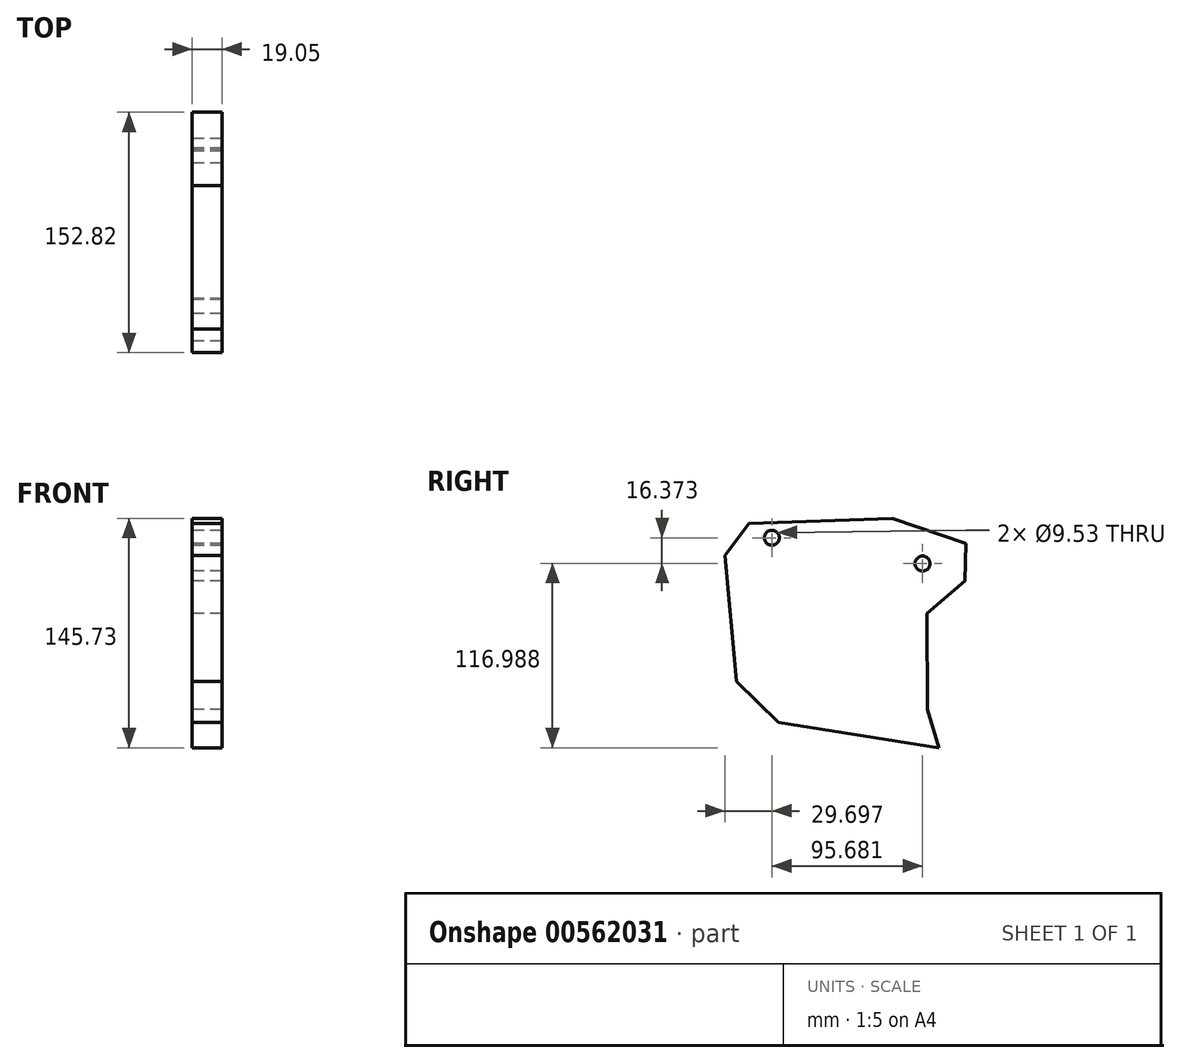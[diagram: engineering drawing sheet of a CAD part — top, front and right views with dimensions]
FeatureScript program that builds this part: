
annotation { "Feature Type Name" : "Feature", "Feature Type Description" : "" }
export const myFeature = defineFeature(function(context is Context, id is Id, definition is map)
    precondition{}
    {
        {
            var Q0;
            Q0=qCreatedBy(makeId("Right.planeOp"),FACE);
            var sketch = newSketch(context, id + "F0", { "sketchPlane" : qUnion([Q0])});
            skLineSegment(sketch, "E0", {"start": v(-513.86, 319.86) * mm, "end": v(-513.86, 78.56) * mm});
            skSolve(sketch);
        }
        {
            var Q0;
            Q0=qCreatedBy(makeId("Right.planeOp"),FACE);
            var sketch = newSketch(context, id + "F1", { "sketchPlane" : qUnion([Q0])});
            skLineSegment(sketch, "E1", {"start": v(-749.74, 255.74) * mm, "end": v(-601.81, 261.03) * mm});
            skLineSegment(sketch, "E2", {"start": v(-562.23, 653.83) * mm, "end": v(-601.81, 261.03) * mm});
            skLineSegment(sketch, "E3", {"start": v(-562.23, 653.83) * mm, "end": v(-749.74, 255.74) * mm});
            skLineSegment(sketch, "E4", {"start": v(-712.77, 291.22) * mm, "end": v(-724.73, 436.34) * mm});
            skLineSegment(sketch, "E5", {"start": v(-712.77, 291.22) * mm, "end": v(-827.95, 541.82) * mm});
            skLineSegment(sketch, "E6", {"start": v(-724.73, 436.34) * mm, "end": v(-827.95, 541.82) * mm});
            skLineSegment(sketch, "E7", {"start": v(-1010.55, 658.15) * mm, "end": v(-827.95, 541.82) * mm});
            skLineSegment(sketch, "E8", {"start": v(-1039.87, 675.04) * mm, "end": v(-1010.55, 658.15) * mm});
            skLineSegment(sketch, "E9", {"start": v(-1039.87, 675.04) * mm, "end": v(-712.77, 291.22) * mm});
            skLineSegment(sketch, "E10", {"start": v(-1010.55, 658.15) * mm, "end": v(-712.77, 291.22) * mm});
            skLineSegment(sketch, "E11", {"start": v(-601.81, 261.03) * mm, "end": v(-596.02, 401.8) * mm});
            skLineSegment(sketch, "E12", {"start": v(-601.81, 261.03) * mm, "end": v(-610.07, 655.83) * mm});
            skLineSegment(sketch, "E13", {"start": v(-596.02, 401.8) * mm, "end": v(-610.07, 655.83) * mm});
            skLineSegment(sketch, "E14", {"start": v(-724.73, 436.34) * mm, "end": v(-596.02, 401.8) * mm});
            skLineSegment(sketch, "E15", {"start": v(-827.95, 541.82) * mm, "end": v(-776.44, 589.47) * mm});
            skLineSegment(sketch, "E16", {"start": v(-749.74, 255.74) * mm, "end": v(-776.44, 589.47) * mm});
            skLineSegment(sketch, "E17", {"start": v(-1044.3, 791.08) * mm, "end": v(-776.44, 589.47) * mm});
            skLineSegment(sketch, "E18", {"start": v(-1392.7, 315.05) * mm, "end": v(-1338.72, 358.03) * mm});
            skLineSegment(sketch, "E19", {"start": v(-1338.72, 358.03) * mm, "end": v(-1297.02, 298.68) * mm});
            skLineSegment(sketch, "E20", {"start": v(-1044.3, 791.08) * mm, "end": v(-1297.02, 298.68) * mm});
            skLineSegment(sketch, "E21", {"start": v(-1297.02, 298.68) * mm, "end": v(-1039.87, 675.04) * mm});
            skLineSegment(sketch, "E22", {"start": v(-1039.87, 675.04) * mm, "end": v(-1044.3, 791.08) * mm});
            skLineSegment(sketch, "E23", {"start": v(-1010.55, 658.15) * mm, "end": v(-1338.72, 358.03) * mm});
            skLineSegment(sketch, "E24", {"start": v(-1392.7, 315.05) * mm, "end": v(-1297.02, 298.68) * mm});
            skLineSegment(sketch, "E25", {"start": v(-1297.02, 298.68) * mm, "end": v(-1297.02, 189.68) * mm});
            skLineSegment(sketch, "E26", {"start": v(-1297.02, 189.68) * mm, "end": v(-1405.13, 208.18) * mm});
            skLineSegment(sketch, "E27", {"start": v(-1405.13, 208.18) * mm, "end": v(-1392.7, 315.05) * mm});
            skLineSegment(sketch, "E28", {"start": v(-1392.7, 315.05) * mm, "end": v(-1297.02, 189.68) * mm});
            skLineSegment(sketch, "E29", {"start": v(0, 0) * mm, "end": v(0, 674.17) * mm});
            skLineSegment(sketch, "E30", {"start": v(-316.61, 320.6) * mm, "end": v(-316.61, 307.94) * mm});
            skLineSegment(sketch, "E31", {"start": v(-400.45, 218.07) * mm, "end": v(-378.01, 218.07) * mm});
            skLineSegment(sketch, "E32", {"start": v(-472.6, 74.76) * mm, "end": v(-472.6, 54.94) * mm});
            skSolve(sketch);
        }
        {
            var Q0;
            Q0=qCreatedBy(makeId("Right.planeOp"),FACE);
            var sketch = newSketch(context, id + "F2", { "sketchPlane" : qUnion([Q0])});
            skLineSegment(sketch, "E33", {"start": v(-1422.4, 303.95) * mm, "end": v(-1415.06, 223.75) * mm});
            skLineSegment(sketch, "E34", {"start": v(-1415.06, 223.75) * mm, "end": v(-1388.66, 197.83) * mm});
            skLineSegment(sketch, "E35", {"start": v(-1388.66, 197.83) * mm, "end": v(-1286.45, 181.7) * mm});
            skLineSegment(sketch, "E36", {"start": v(-1286.45, 181.7) * mm, "end": v(-1293.79, 206.14) * mm});
            skLineSegment(sketch, "E37", {"start": v(-1293.79, 206.14) * mm, "end": v(-1294.28, 267.03) * mm});
            skLineSegment(sketch, "E38", {"start": v(-1294.28, 267.03) * mm, "end": v(-1270.07, 287.56) * mm});
            skLineSegment(sketch, "E39", {"start": v(-1270.07, 287.56) * mm, "end": v(-1269.58, 311.28) * mm});
            skLineSegment(sketch, "E40", {"start": v(-1269.58, 311.28) * mm, "end": v(-1316.28, 327.42) * mm});
            skLineSegment(sketch, "E41", {"start": v(-1316.28, 327.42) * mm, "end": v(-1407.37, 324.03) * mm});
            skLineSegment(sketch, "E42", {"start": v(-1407.37, 324.03) * mm, "end": v(-1422.4, 303.95) * mm});
            skCircle(sketch, "E43", {"center": v(-1392.7, 315.05) * mm, "radius": 4.76 * mm});
            skCircle(sketch, "E44", {"center": v(-1297.02, 298.68) * mm, "radius": 4.76 * mm});
            skSolve(sketch);
        }
        {
            var Q0;
            Q0 = qSketchRegion(id + "F2", true);
            extrude(context, id + "F3", {"entities" : qUnion([Q0]), "depth" : 19.05 * mm, "offsetDistance" : 25.4 * mm});
        }
    });
